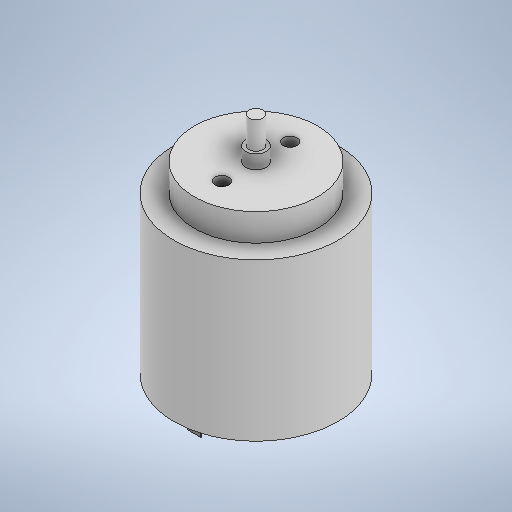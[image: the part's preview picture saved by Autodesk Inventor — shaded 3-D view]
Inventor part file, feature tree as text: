
AUTODESK INVENTOR PART (.ipt)
format: ipt  version: 2025.2 (Build 292293000, 293)  size: 280,576 bytes
history: native  units: mm
features: extrude x8, sketch x8
ambient origin geometry x8: Origin, YZ Plane, XZ Plane, XY Plane, X Axis, Y Axis, Z Axis, Center Point
bodies: Solid1 (feature_tree)
feature tree (16):
  extrude  "Extrusion1"  Depth=23.0mm TaperAngle=0.0deg
  extrude  "Extrusion2"  Depth=4.0mm TaperAngle=0.0deg
  extrude  "Extrusion3"  Depth=3.0mm
  extrude  "Extrusion4"  Depth=6.0mm TaperAngle=0.0deg
  extrude  "Extrusion5"  Depth=2.0mm
  extrude  "Extrusion6"  Depth=4.0mm
  extrude  "Extrusion7"  Depth=2.0mm
  extrude  "Extrusion8"  Depth=2.0mm
  sketch  "Sketch1"  dims[d0=24.0mm d1=23.0mm d2=0.0mm]
  sketch  "Sketch2"  dims[d3=18.0mm d4=4.0mm d5=0.0mm]
  sketch  "Sketch3"  dims[d6=2.0mm d7=3.0mm]
  sketch  "Sketch4"  dims[d8=2.0mm d9=0.0mm d10=6.0mm d11=0.0mm]
  sketch  "Sketch5"  dims[d12=2.0mm d13=2.0mm]
  sketch  "Sketch6"  dims[d14=3.0mm d15=0.0mm d16=4.0mm]
  sketch  "Sketch7"  dims[d17=1.0mm d18=0.0mm d19=2.0mm]
  sketch  "Sketch8"  dims[d20=0.2mm d21=0.0mm d22=2.0mm d23=2.0mm d24=2.0mm d25=0.0mm]
